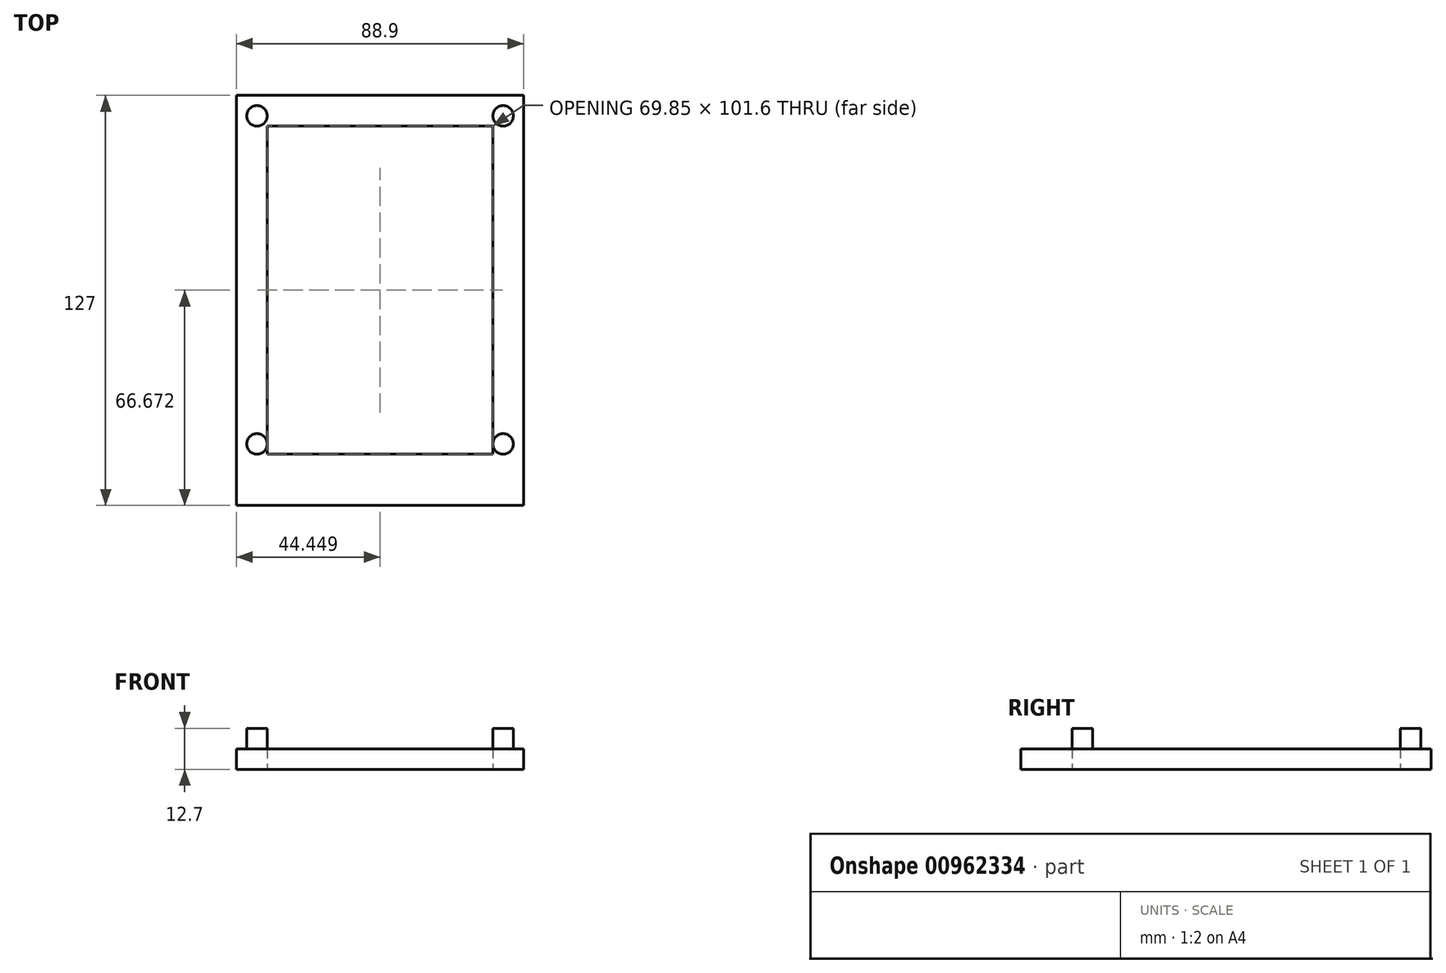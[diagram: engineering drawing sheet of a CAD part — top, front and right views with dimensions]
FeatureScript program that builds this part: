
annotation { "Feature Type Name" : "Feature", "Feature Type Description" : "" }
export const myFeature = defineFeature(function(context is Context, id is Id, definition is map)
    precondition{}
    {
        {
            var Q0;
            Q0=qCreatedBy(makeId("Top.planeOp"),FACE);
            var sketch = newSketch(context, id + "F0", { "sketchPlane" : qUnion([Q0])});
            skLineSegment(sketch, "E0.bottom", {"start": v(-65.23, -50.84) * mm, "end": v(23.67, -50.84) * mm});
            skLineSegment(sketch, "E0.top", {"start": v(-65.23, 76.16) * mm, "end": v(23.67, 76.16) * mm});
            skLineSegment(sketch, "E0.left", {"start": v(-65.23, -50.84) * mm, "end": v(-65.23, 76.16) * mm});
            skLineSegment(sketch, "E0.right", {"start": v(23.67, -50.84) * mm, "end": v(23.67, 76.16) * mm});
            skLineSegment(sketch, "E1.bottom", {"start": v(-55.7, -34.97) * mm, "end": v(14.14, -34.97) * mm});
            skLineSegment(sketch, "E1.top", {"start": v(-55.7, 66.63) * mm, "end": v(14.14, 66.63) * mm});
            skLineSegment(sketch, "E1.left", {"start": v(-55.7, -34.97) * mm, "end": v(-55.7, 66.63) * mm});
            skLineSegment(sketch, "E1.right", {"start": v(14.14, -34.97) * mm, "end": v(14.14, 66.63) * mm});
            skSolve(sketch);
        }
        {
            var Q0;
            Q0 = qSketchRegion(id + "F0", true);
            extrude(context, id + "F1", {"entities" : qUnion([Q0]), "depth" : 6.35 * mm, "offsetDistance" : 25.4 * mm});
        }
        {
            var Q0;
            Q0=makeQuery(id+"F1.opExtrude","CAP_FACE",FACE,{"disambiguationData":[OSD([sQuery(id+"F0.wireOp",EDGE,"E0.bottom"),sQuery(id+"F0.wireOp",EDGE,"E0.top"),sQuery(id+"F0.wireOp",EDGE,"E0.left"),sQuery(id+"F0.wireOp",EDGE,"E0.right"),sQuery(id+"F0.wireOp",EDGE,"E1.bottom"),sQuery(id+"F0.wireOp",EDGE,"E1.top"),sQuery(id+"F0.wireOp",EDGE,"E1.left"),sQuery(id+"F0.wireOp",EDGE,"E1.right")])],"isStart":false});
            var sketch = newSketch(context, id + "F2", { "sketchPlane" : qUnion([Q0])});
            skCircle(sketch, "E2", {"center": v(-58.88, 69.8) * mm, "radius": 3.18 * mm});
            skCircle(sketch, "E3", {"center": v(-58.88, -31.8) * mm, "radius": 3.18 * mm});
            skCircle(sketch, "E4", {"center": v(17.32, 69.8) * mm, "radius": 3.18 * mm});
            skCircle(sketch, "E5", {"center": v(17.32, -31.8) * mm, "radius": 3.17 * mm});
            skSolve(sketch);
        }
        {
            var Q0;
            Q0 = qSketchRegion(id + "F2", true);
            extrude(context, id + "F3", {"entities" : qUnion([Q0]), "operationType" : NewBodyOperationType.ADD, "depth" : 6.35 * mm, "offsetDistance" : 25.4 * mm});
        }
    });
